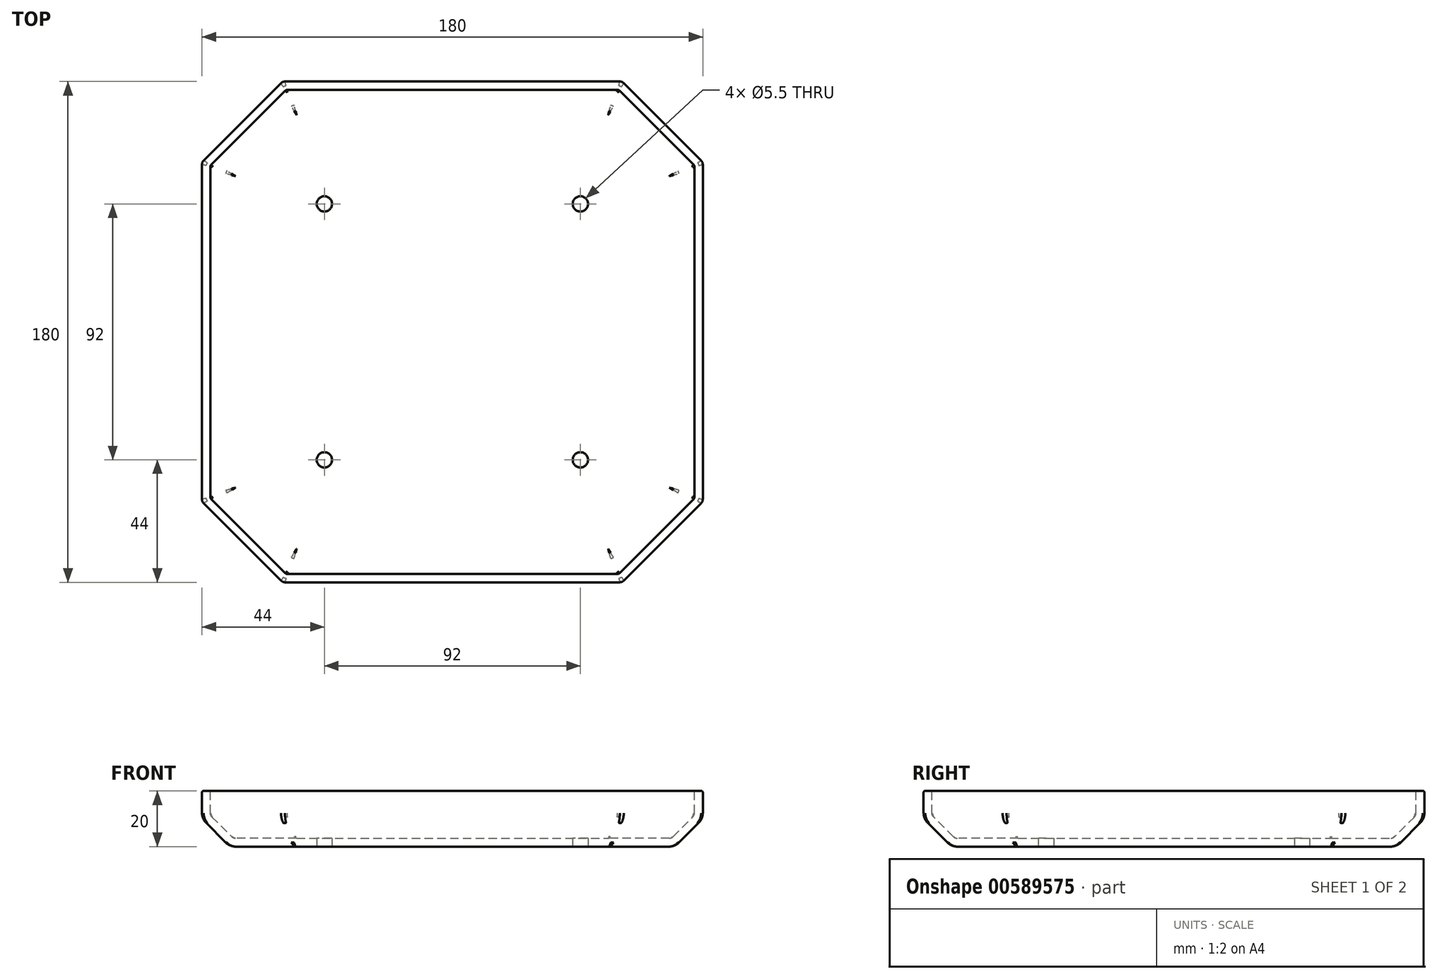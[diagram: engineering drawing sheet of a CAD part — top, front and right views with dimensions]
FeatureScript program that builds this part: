
annotation { "Feature Type Name" : "Feature", "Feature Type Description" : "" }
export const myFeature = defineFeature(function(context is Context, id is Id, definition is map)
    precondition{}
    {
        {
            var Q0;
            Q0=qCreatedBy(makeId("Top.planeOp"),FACE);
            var sketch = newSketch(context, id + "F0", { "sketchPlane" : qUnion([Q0])});
            skLineSegment(sketch, "E0.bottom", {"start": v(-61, 90) * mm, "end": v(61, 90) * mm});
            skLineSegment(sketch, "E0.top", {"start": v(-61, -90) * mm, "end": v(61, -90) * mm});
            skLineSegment(sketch, "E0.left", {"start": v(-90, 61) * mm, "end": v(-90, -61) * mm});
            skLineSegment(sketch, "E0.right", {"start": v(90, 61) * mm, "end": v(90, -61) * mm});
            skLineSegment(sketch, "E1", {"start": v(0, 156.9) * mm, "end": v(0, -146.72) * mm, "construction": true});
            skLineSegment(sketch, "E2", {"start": v(-149.43, 0) * mm, "end": v(169.81, 0) * mm, "construction": true});
            skLineSegment(sketch, "E3", {"start": v(-90, 61) * mm, "end": v(-61, 90) * mm});
            skLineSegment(sketch, "E4", {"start": v(-90, -61) * mm, "end": v(-61, -90) * mm});
            skLineSegment(sketch, "E5", {"start": v(61, -90) * mm, "end": v(90, -61) * mm});
            skLineSegment(sketch, "E6", {"start": v(61, 90) * mm, "end": v(90, 61) * mm});
            skPoint(sketch, "E7.orphan", {"position": v(-90, 90) * mm});
            skPoint(sketch, "E8.orphan", {"position": v(90, 90) * mm});
            skPoint(sketch, "E9.orphan", {"position": v(90, -90) * mm});
            skPoint(sketch, "E10.orphan", {"position": v(-90, -90) * mm});
            skSolve(sketch);
        }
        {
            var Q0;
            Q0=qSketchRegion(id+"F0",true);
            extrude(context, id + "F1", {"entities" : qUnion([Q0]), "depth" : 20 * mm, "offsetDistance" : 25 * mm});
        }
        {
            var Q0;
            Q0=makeQuery(id+"F1.opExtrude","CAP_EDGE",EDGE,{"disambiguationData":[OSD([sQuery(id+"F0.wireOp",EDGE,"E0.top")])],"isStart":true});
            var Q1;
            Q1=makeQuery(id+"F1.opExtrude","CAP_EDGE",EDGE,{"disambiguationData":[OSD([sQuery(id+"F0.wireOp",EDGE,"E4")])],"isStart":true});
            var Q2;
            Q2=makeQuery(id+"F1.opExtrude","CAP_EDGE",EDGE,{"disambiguationData":[OSD([sQuery(id+"F0.wireOp",EDGE,"E0.left")])],"isStart":true});
            var Q3;
            Q3=makeQuery(id+"F1.opExtrude","CAP_EDGE",EDGE,{"disambiguationData":[OSD([sQuery(id+"F0.wireOp",EDGE,"E3")])],"isStart":true});
            var Q4;
            Q4=makeQuery(id+"F1.opExtrude","CAP_EDGE",EDGE,{"disambiguationData":[OSD([sQuery(id+"F0.wireOp",EDGE,"E0.bottom")])],"isStart":true});
            var Q5;
            Q5=makeQuery(id+"F1.opExtrude","CAP_EDGE",EDGE,{"disambiguationData":[OSD([sQuery(id+"F0.wireOp",EDGE,"E6")])],"isStart":true});
            var Q6;
            Q6=makeQuery(id+"F1.opExtrude","CAP_EDGE",EDGE,{"disambiguationData":[OSD([sQuery(id+"F0.wireOp",EDGE,"E0.right")])],"isStart":true});
            var Q7;
            Q7=makeQuery(id+"F1.opExtrude","CAP_EDGE",EDGE,{"disambiguationData":[OSD([sQuery(id+"F0.wireOp",EDGE,"E5")])],"isStart":true});
            chamfer(context, id + "F2", {"entities" : qUnion([Q0, Q1, Q2, Q3, Q4, Q5, Q6, Q7]), "chamferType" : ChamferType.TWO_OFFSETS, "width1" : 10 * mm, "oppositeDirection" : true, "width2" : 10 * mm, "tangentPropagation" : true});
        }
        {
            var Q0;
            {var subQ0=sQuery(id+"F0.wireOp",EDGE,"E6");Q0=makeQuery(id+"F2.opChamfer","BLEND_EDGE",EDGE,{"blendedFrom":[makeQuery(id+"F1.opExtrude","CAP_EDGE",EDGE,{"disambiguationData":[OSD([subQ0])],"isStart":true}),makeQuery(id+"F1.opExtrude","SWEPT_FACE",FACE,{"disambiguationData":[OSD([subQ0])]})],"blendedInto":[makeQuery(id+"F1.opExtrude","SWEPT_FACE",FACE,{"disambiguationData":[OSD([subQ0])]})]});}
            var Q1;
            {var subQ0=sQuery(id+"F0.wireOp",EDGE,"E0.right");Q1=makeQuery(id+"F2.opChamfer","BLEND_EDGE",EDGE,{"blendedFrom":[makeQuery(id+"F1.opExtrude","CAP_EDGE",EDGE,{"disambiguationData":[OSD([subQ0])],"isStart":true}),makeQuery(id+"F1.opExtrude","SWEPT_FACE",FACE,{"disambiguationData":[OSD([subQ0])]})],"blendedInto":[makeQuery(id+"F1.opExtrude","SWEPT_FACE",FACE,{"disambiguationData":[OSD([subQ0])]})]});}
            var Q2;
            {var subQ0=sQuery(id+"F0.wireOp",EDGE,"E5");Q2=makeQuery(id+"F2.opChamfer","BLEND_EDGE",EDGE,{"blendedFrom":[makeQuery(id+"F1.opExtrude","CAP_EDGE",EDGE,{"disambiguationData":[OSD([subQ0])],"isStart":true}),makeQuery(id+"F1.opExtrude","SWEPT_FACE",FACE,{"disambiguationData":[OSD([subQ0])]})],"blendedInto":[makeQuery(id+"F1.opExtrude","SWEPT_FACE",FACE,{"disambiguationData":[OSD([subQ0])]})]});}
            var Q3;
            {var subQ0=sQuery(id+"F0.wireOp",EDGE,"E0.top");Q3=makeQuery(id+"F2.opChamfer","BLEND_EDGE",EDGE,{"blendedFrom":[makeQuery(id+"F1.opExtrude","CAP_EDGE",EDGE,{"disambiguationData":[OSD([subQ0])],"isStart":true}),makeQuery(id+"F1.opExtrude","SWEPT_FACE",FACE,{"disambiguationData":[OSD([subQ0])]})],"blendedInto":[makeQuery(id+"F1.opExtrude","SWEPT_FACE",FACE,{"disambiguationData":[OSD([subQ0])]})]});}
            var Q4;
            {var subQ0=sQuery(id+"F0.wireOp",EDGE,"E4");Q4=makeQuery(id+"F2.opChamfer","BLEND_EDGE",EDGE,{"blendedFrom":[makeQuery(id+"F1.opExtrude","CAP_EDGE",EDGE,{"disambiguationData":[OSD([subQ0])],"isStart":true}),makeQuery(id+"F1.opExtrude","SWEPT_FACE",FACE,{"disambiguationData":[OSD([subQ0])]})],"blendedInto":[makeQuery(id+"F1.opExtrude","SWEPT_FACE",FACE,{"disambiguationData":[OSD([subQ0])]})]});}
            var Q5;
            {var subQ0=sQuery(id+"F0.wireOp",EDGE,"E0.left");Q5=makeQuery(id+"F2.opChamfer","BLEND_EDGE",EDGE,{"blendedFrom":[makeQuery(id+"F1.opExtrude","CAP_EDGE",EDGE,{"disambiguationData":[OSD([subQ0])],"isStart":true}),makeQuery(id+"F1.opExtrude","SWEPT_FACE",FACE,{"disambiguationData":[OSD([subQ0])]})],"blendedInto":[makeQuery(id+"F1.opExtrude","SWEPT_FACE",FACE,{"disambiguationData":[OSD([subQ0])]})]});}
            var Q6;
            {var subQ0=sQuery(id+"F0.wireOp",EDGE,"E3");Q6=makeQuery(id+"F2.opChamfer","BLEND_EDGE",EDGE,{"blendedFrom":[makeQuery(id+"F1.opExtrude","CAP_EDGE",EDGE,{"disambiguationData":[OSD([subQ0])],"isStart":true}),makeQuery(id+"F1.opExtrude","SWEPT_FACE",FACE,{"disambiguationData":[OSD([subQ0])]})],"blendedInto":[makeQuery(id+"F1.opExtrude","SWEPT_FACE",FACE,{"disambiguationData":[OSD([subQ0])]})]});}
            var Q7;
            {var subQ0=sQuery(id+"F0.wireOp",EDGE,"E0.bottom");Q7=makeQuery(id+"F2.opChamfer","BLEND_EDGE",EDGE,{"blendedFrom":[makeQuery(id+"F1.opExtrude","CAP_EDGE",EDGE,{"disambiguationData":[OSD([subQ0])],"isStart":true}),makeQuery(id+"F1.opExtrude","SWEPT_FACE",FACE,{"disambiguationData":[OSD([subQ0])]})],"blendedInto":[makeQuery(id+"F1.opExtrude","SWEPT_FACE",FACE,{"disambiguationData":[OSD([subQ0])]})]});}
            fillet(context, id + "F3", {"entities" : qUnion([Q0, Q1, Q2, Q3, Q4, Q5, Q6, Q7]), "radius" : 5 * mm, "tangentPropagation" : true, "allowEdgeOverflow" : false});
        }
        {
            var Q0;
            Q0=makeQuery(id+"FPPhOqti1fwxr9W_1.boolean.opBoolean","MERGE",EDGE,{"derivedFrom":[makeQuery(id+"F1.opExtrude","SWEPT_EDGE",EDGE,{"disambiguationData":[OSD([sQuery(id+"F0.wireOp",EDGE,"E0.bottom"),sQuery(id+"F0.wireOp",EDGE,"E6")])]}),makeQuery(id+"FPPhOqti1fwxr9W_1.opExtrude","SWEPT_EDGE",EDGE,{"disambiguationData":[OSD([sQuery(id+"Fz5JRvEoveer3CH_1.wireOp",EDGE,"2a3d6910-861b-4cd5-9b03-4775f4baa4122.MirrorCS"),sQuery(id+"Fz5JRvEoveer3CH_1.wireOp",EDGE,"2a3d6910-861b-4cd5-9b03-4775f4baa4128.MirrorCS")])]})]});
            var Q1;
            Q1=makeQuery(id+"FPPhOqti1fwxr9W_1.boolean.opBoolean","MERGE",EDGE,{"derivedFrom":[makeQuery(id+"F1.opExtrude","SWEPT_EDGE",EDGE,{"disambiguationData":[OSD([sQuery(id+"F0.wireOp",EDGE,"E0.right"),sQuery(id+"F0.wireOp",EDGE,"E6")])]}),makeQuery(id+"FPPhOqti1fwxr9W_1.opExtrude","SWEPT_EDGE",EDGE,{"disambiguationData":[OSD([sQuery(id+"Fz5JRvEoveer3CH_1.wireOp",EDGE,"2a3d6910-861b-4cd5-9b03-4775f4baa4123.MirrorCS"),sQuery(id+"Fz5JRvEoveer3CH_1.wireOp",EDGE,"2a3d6910-861b-4cd5-9b03-4775f4baa4128.MirrorCS")])]})]});
            var Q2;
            Q2=makeQuery(id+"FPPhOqti1fwxr9W_1.boolean.opBoolean","MERGE",EDGE,{"derivedFrom":[makeQuery(id+"F1.opExtrude","SWEPT_EDGE",EDGE,{"disambiguationData":[OSD([sQuery(id+"F0.wireOp",EDGE,"E0.bottom"),sQuery(id+"F0.wireOp",EDGE,"E3")])]}),makeQuery(id+"FPPhOqti1fwxr9W_1.opExtrude","SWEPT_EDGE",EDGE,{"disambiguationData":[OSD([sQuery(id+"Fz5JRvEoveer3CH_1.wireOp",EDGE,"ed581da2-8291-48fe-b3ed-69cef9aa138a21.MirrorCS"),sQuery(id+"Fz5JRvEoveer3CH_1.wireOp",EDGE,"ed581da2-8291-48fe-b3ed-69cef9aa138a29.MirrorCS")])]})]});
            var Q3;
            Q3=makeQuery(id+"FPPhOqti1fwxr9W_1.boolean.opBoolean","MERGE",EDGE,{"derivedFrom":[makeQuery(id+"F1.opExtrude","SWEPT_EDGE",EDGE,{"disambiguationData":[OSD([sQuery(id+"F0.wireOp",EDGE,"E0.right"),sQuery(id+"F0.wireOp",EDGE,"E5")])]}),makeQuery(id+"FPPhOqti1fwxr9W_1.opExtrude","SWEPT_EDGE",EDGE,{"disambiguationData":[OSD([sQuery(id+"Fz5JRvEoveer3CH_1.wireOp",EDGE,"ipMyZAYz-hxr7-lcg5-t2S8-iXpkemTBpe0R"),sQuery(id+"Fz5JRvEoveer3CH_1.wireOp",EDGE,"9DZyxgSF-dPzx-yPfH-Wviq-A2BslGx0M5Kc")])]})]});
            var Q4;
            Q4=makeQuery(id+"F2.opChamfer","BLEND_EDGE",EDGE,{"blendedFrom":[makeQuery(id+"F1.opExtrude","CAP_EDGE",EDGE,{"disambiguationData":[OSD([sQuery(id+"F0.wireOp",EDGE,"E0.top")])],"isStart":true}),makeQuery(id+"F1.opExtrude","CAP_EDGE",EDGE,{"disambiguationData":[OSD([sQuery(id+"F0.wireOp",EDGE,"E5")])],"isStart":true})],"blendedInto":[]});
            var Q5;
            Q5=makeQuery(id+"F2.opChamfer","BLEND_EDGE",EDGE,{"blendedFrom":[makeQuery(id+"F1.opExtrude","CAP_EDGE",EDGE,{"disambiguationData":[OSD([sQuery(id+"F0.wireOp",EDGE,"E0.top")])],"isStart":true}),makeQuery(id+"F1.opExtrude","CAP_EDGE",EDGE,{"disambiguationData":[OSD([sQuery(id+"F0.wireOp",EDGE,"E4")])],"isStart":true})],"blendedInto":[]});
            var Q6;
            Q6=makeQuery(id+"F2.opChamfer","BLEND_EDGE",EDGE,{"blendedFrom":[makeQuery(id+"F1.opExtrude","CAP_EDGE",EDGE,{"disambiguationData":[OSD([sQuery(id+"F0.wireOp",EDGE,"E0.left")])],"isStart":true}),makeQuery(id+"F1.opExtrude","CAP_EDGE",EDGE,{"disambiguationData":[OSD([sQuery(id+"F0.wireOp",EDGE,"E4")])],"isStart":true})],"blendedInto":[]});
            var Q7;
            Q7=makeQuery(id+"F2.opChamfer","BLEND_EDGE",EDGE,{"blendedFrom":[makeQuery(id+"F1.opExtrude","CAP_EDGE",EDGE,{"disambiguationData":[OSD([sQuery(id+"F0.wireOp",EDGE,"E0.left")])],"isStart":true}),makeQuery(id+"F1.opExtrude","CAP_EDGE",EDGE,{"disambiguationData":[OSD([sQuery(id+"F0.wireOp",EDGE,"E3")])],"isStart":true})],"blendedInto":[]});
            fillet(context, id + "F4", {"entities" : qUnion([Q0, Q1, Q2, Q3, Q4, Q5, Q6, Q7]), "radius" : 2 * mm, "tangentPropagation" : true, "allowEdgeOverflow" : false});
        }
        {
            var Q0;
            {var subQ0=sQuery(id+"F0.wireOp",EDGE,"E0.left");Q0=makeQuery(id+"F2.opChamfer","BLEND_EDGE",EDGE,{"blendedFrom":[makeQuery(id+"F1.opExtrude","CAP_EDGE",EDGE,{"disambiguationData":[OSD([subQ0])],"isStart":true}),makeQuery(id+"F1.opExtrude","CAP_FACE",FACE,{"disambiguationData":[OSD([sQuery(id+"F0.wireOp",EDGE,"E0.bottom"),sQuery(id+"F0.wireOp",EDGE,"E0.top"),subQ0,sQuery(id+"F0.wireOp",EDGE,"E0.right"),sQuery(id+"F0.wireOp",EDGE,"E3"),sQuery(id+"F0.wireOp",EDGE,"E4"),sQuery(id+"F0.wireOp",EDGE,"E5"),sQuery(id+"F0.wireOp",EDGE,"E6")])],"isStart":true})],"blendedInto":[makeQuery(id+"F1.opExtrude","CAP_FACE",FACE,{"disambiguationData":[OSD([sQuery(id+"F0.wireOp",EDGE,"E0.bottom"),sQuery(id+"F0.wireOp",EDGE,"E0.top"),subQ0,sQuery(id+"F0.wireOp",EDGE,"E0.right"),sQuery(id+"F0.wireOp",EDGE,"E3"),sQuery(id+"F0.wireOp",EDGE,"E4"),sQuery(id+"F0.wireOp",EDGE,"E5"),sQuery(id+"F0.wireOp",EDGE,"E6")])],"isStart":true})]});}
            fillet(context, id + "F5", {"entities" : qUnion([Q0]), "radius" : 5 * mm, "tangentPropagation" : true, "allowEdgeOverflow" : false});
        }
        {
            var Q0;
            Q0=makeQuery(id+"F1.opExtrude","CAP_FACE",FACE,{"disambiguationData":[OSD([sQuery(id+"F0.wireOp",EDGE,"E0.bottom"),sQuery(id+"F0.wireOp",EDGE,"E0.top"),sQuery(id+"F0.wireOp",EDGE,"E0.left"),sQuery(id+"F0.wireOp",EDGE,"E0.right"),sQuery(id+"F0.wireOp",EDGE,"E3"),sQuery(id+"F0.wireOp",EDGE,"E4"),sQuery(id+"F0.wireOp",EDGE,"E5"),sQuery(id+"F0.wireOp",EDGE,"E6")])],"isStart":false});
            shell(context, id + "F6", {"entities" : qUnion([Q0]), "thickness" : 3 * mm});
        }
        {
            var Q0;
            Q0=makeQuery(id+"F1.opExtrude","CAP_FACE",FACE,{"disambiguationData":[OSD([sQuery(id+"F0.wireOp",EDGE,"E0.bottom"),sQuery(id+"F0.wireOp",EDGE,"E0.top"),sQuery(id+"F0.wireOp",EDGE,"E0.left"),sQuery(id+"F0.wireOp",EDGE,"E0.right"),sQuery(id+"F0.wireOp",EDGE,"E3"),sQuery(id+"F0.wireOp",EDGE,"E4"),sQuery(id+"F0.wireOp",EDGE,"E5"),sQuery(id+"F0.wireOp",EDGE,"E6")])],"isStart":true});
            var sketch = newSketch(context, id + "F7", { "sketchPlane" : qUnion([Q0])});
            skLineSegment(sketch, "E11", {"start": v(0, 77.93) * mm, "end": v(0, -77.93) * mm, "construction": true});
            skLineSegment(sketch, "E12", {"start": v(-77.93, 0) * mm, "end": v(77.93, 0) * mm, "construction": true});
            skLineSegment(sketch, "E13", {"start": v(-66.96, -66.96) * mm, "end": v(66.96, 66.96) * mm, "construction": true});
            skLineSegment(sketch, "E14", {"start": v(-66.96, 66.96) * mm, "end": v(66.96, -66.96) * mm, "construction": true});
            skCircle(sketch, "E15", {"center": v(-46, -46) * mm, "radius": 2.75 * mm});
            skCircle(sketch, "E16", {"center": v(-46, 46) * mm, "radius": 2.75 * mm});
            skCircle(sketch, "E17", {"center": v(46, 46) * mm, "radius": 2.75 * mm});
            skCircle(sketch, "E18", {"center": v(46, -46) * mm, "radius": 2.75 * mm});
            skSolve(sketch);
        }
        {
            var Q0;
            Q0=qSketchRegion(id+"F7",true);
            extrude(context, id + "F8", {"entities" : qUnion([Q0]), "operationType" : NewBodyOperationType.REMOVE, "oppositeDirection" : true, "depth" : 25 * mm});
        }
        {
            var Q0;
            Q0=makeQuery(id+"F1.opExtrude","CAP_EDGE",EDGE,{"disambiguationData":[OSD([sQuery(id+"F0.wireOp",EDGE,"E0.bottom")])],"isStart":false});
            fillet(context, id + "F9", {"entities" : qUnion([Q0]), "radius" : 0.5 * mm, "tangentPropagation" : true, "allowEdgeOverflow" : false});
        }
        {
            var Q0;
            {var subQ0=sQuery(id+"Fz5JRvEoveer3CH_1.wireOp",EDGE,"2a3d6910-861b-4cd5-9b03-4775f4baa4123.MirrorCS");var subQ1=sQuery(id+"Fz5JRvEoveer3CH_1.wireOp",EDGE,"9DZyxgSF-dPzx-yPfH-Wviq-A2BslGx0M5Kc");var subQ2=sQuery(id+"F0.wireOp",EDGE,"E0.right");var subQ4=sQuery(id+"Fz5JRvEoveer3CH_1.wireOp",EDGE,"2a3d6910-861b-4cd5-9b03-4775f4baa4128.MirrorCS");var subQ5=sQuery(id+"F0.wireOp",EDGE,"E6");var subQ7=makeQuery(id+"F6.opShell","OFFSET_EDGE",EDGE,{"disambiguationData":[OSD([subQ2,subQ5,subQ1,subQ0,subQ4])]});Q0=makeQuery(id+"FdvM71XXdWx955j_1.boolean.opBoolean","MERGE",EDGE,{"derivedFrom":[makeQuery(id+"Fx6GF23n7295V4c_1.boolean.opBoolean","SPLIT",EDGE,{"disambiguationData":[TD([makeQuery(id+"Fx6GF23n7295V4c_1.opExtrude","SWEPT_FACE",FACE,{"disambiguationData":[OSD([sQuery(id+"F88hl3kOj6oPiEs_1.wireOp",EDGE,"Me13D1SK-nVIm-EUZ4-u9ei-o20qw3bNrjn4.top")])]})])],"derivedFrom":subQ7}),makeQuery(id+"Fx6GF23n7295V4c_1.boolean.opBoolean","SPLIT",EDGE,{"disambiguationData":[TD([makeQuery(id+"Fx6GF23n7295V4c_1.opExtrude","SWEPT_FACE",FACE,{"disambiguationData":[OSD([sQuery(id+"F88hl3kOj6oPiEs_1.wireOp",EDGE,"SEwAjyqW-bpiv-PUip-ikyk-NmgX0KRneyY1.bottom")])]})])],"derivedFrom":subQ7}),makeQuery(id+"Fx6GF23n7295V4c_1.boolean.opBoolean","SPLIT",EDGE,{"disambiguationData":[TD([makeQuery(id+"Fx6GF23n7295V4c_1.opExtrude","SWEPT_FACE",FACE,{"disambiguationData":[OSD([sQuery(id+"F88hl3kOj6oPiEs_1.wireOp",EDGE,"Me13D1SK-nVIm-EUZ4-u9ei-o20qw3bNrjn4.bottom")])]})])],"derivedFrom":subQ7}),makeQuery(id+"FdvM71XXdWx955j_1.opExtrude","SWEPT_EDGE",EDGE,{"disambiguationData":[OSD([sQuery(id+"FbjQCpLspRogReH_1.wireOp",EDGE,"f59d4a9d-c009-47c2-b376-d2920ef91a05.8"),sQuery(id+"FbjQCpLspRogReH_1.wireOp",EDGE,"bRIcUt5c-2wkI-2ICm-p1hK-NbXWkc9YcS5q")])]})]});}
            var Q1;
            {var subQ0=sQuery(id+"Fz5JRvEoveer3CH_1.wireOp",EDGE,"ed581da2-8291-48fe-b3ed-69cef9aa138a21.MirrorCS");var subQ1=sQuery(id+"Fz5JRvEoveer3CH_1.wireOp",EDGE,"2a3d6910-861b-4cd5-9b03-4775f4baa4122.MirrorCS");var subQ2=sQuery(id+"F0.wireOp",EDGE,"E0.bottom");var subQ4=sQuery(id+"Fz5JRvEoveer3CH_1.wireOp",EDGE,"2a3d6910-861b-4cd5-9b03-4775f4baa4128.MirrorCS");var subQ5=sQuery(id+"F0.wireOp",EDGE,"E6");var subQ7=makeQuery(id+"F6.opShell","OFFSET_EDGE",EDGE,{"disambiguationData":[OSD([subQ2,subQ5,subQ1,subQ4,subQ0])]});Q1=makeQuery(id+"FdvM71XXdWx955j_1.boolean.opBoolean","MERGE",EDGE,{"derivedFrom":[makeQuery(id+"Fx6GF23n7295V4c_1.boolean.opBoolean","SPLIT",EDGE,{"disambiguationData":[TD([makeQuery(id+"Fx6GF23n7295V4c_1.opExtrude","SWEPT_FACE",FACE,{"disambiguationData":[OSD([sQuery(id+"F88hl3kOj6oPiEs_1.wireOp",EDGE,"Me13D1SK-nVIm-EUZ4-u9ei-o20qw3bNrjn4.top")])]})])],"derivedFrom":subQ7}),makeQuery(id+"Fx6GF23n7295V4c_1.boolean.opBoolean","SPLIT",EDGE,{"disambiguationData":[TD([makeQuery(id+"Fx6GF23n7295V4c_1.opExtrude","SWEPT_FACE",FACE,{"disambiguationData":[OSD([sQuery(id+"F88hl3kOj6oPiEs_1.wireOp",EDGE,"SEwAjyqW-bpiv-PUip-ikyk-NmgX0KRneyY1.bottom")])]})])],"derivedFrom":subQ7}),makeQuery(id+"Fx6GF23n7295V4c_1.boolean.opBoolean","SPLIT",EDGE,{"disambiguationData":[TD([makeQuery(id+"Fx6GF23n7295V4c_1.opExtrude","SWEPT_FACE",FACE,{"disambiguationData":[OSD([sQuery(id+"F88hl3kOj6oPiEs_1.wireOp",EDGE,"Me13D1SK-nVIm-EUZ4-u9ei-o20qw3bNrjn4.bottom")])]})])],"derivedFrom":subQ7}),makeQuery(id+"FdvM71XXdWx955j_1.opExtrude","SWEPT_EDGE",EDGE,{"disambiguationData":[OSD([sQuery(id+"FbjQCpLspRogReH_1.wireOp",EDGE,"f59d4a9d-c009-47c2-b376-d2920ef91a05.4"),sQuery(id+"FbjQCpLspRogReH_1.wireOp",EDGE,"bRIcUt5c-2wkI-2ICm-p1hK-NbXWkc9YcS5q")])]})]});}
            var Q2;
            {var subQ0=sQuery(id+"Fz5JRvEoveer3CH_1.wireOp",EDGE,"2a3d6910-861b-4cd5-9b03-4775f4baa4123.MirrorCS");var subQ1=sQuery(id+"Fz5JRvEoveer3CH_1.wireOp",EDGE,"9DZyxgSF-dPzx-yPfH-Wviq-A2BslGx0M5Kc");var subQ2=sQuery(id+"F0.wireOp",EDGE,"E0.right");var subQ4=sQuery(id+"Fz5JRvEoveer3CH_1.wireOp",EDGE,"ipMyZAYz-hxr7-lcg5-t2S8-iXpkemTBpe0R");var subQ5=sQuery(id+"F0.wireOp",EDGE,"E5");var subQ7=makeQuery(id+"F6.opShell","OFFSET_EDGE",EDGE,{"disambiguationData":[OSD([subQ2,subQ5,subQ4,subQ1,subQ0])]});Q2=makeQuery(id+"FdvM71XXdWx955j_1.boolean.opBoolean","MERGE",EDGE,{"derivedFrom":[makeQuery(id+"Fx6GF23n7295V4c_1.boolean.opBoolean","SPLIT",EDGE,{"disambiguationData":[TD([makeQuery(id+"Fx6GF23n7295V4c_1.opExtrude","SWEPT_FACE",FACE,{"disambiguationData":[OSD([sQuery(id+"F88hl3kOj6oPiEs_1.wireOp",EDGE,"Me13D1SK-nVIm-EUZ4-u9ei-o20qw3bNrjn4.top")])]})])],"derivedFrom":subQ7}),makeQuery(id+"Fx6GF23n7295V4c_1.boolean.opBoolean","SPLIT",EDGE,{"disambiguationData":[TD([makeQuery(id+"Fx6GF23n7295V4c_1.opExtrude","SWEPT_FACE",FACE,{"disambiguationData":[OSD([sQuery(id+"F88hl3kOj6oPiEs_1.wireOp",EDGE,"SEwAjyqW-bpiv-PUip-ikyk-NmgX0KRneyY1.bottom")])]})])],"derivedFrom":subQ7}),makeQuery(id+"Fx6GF23n7295V4c_1.boolean.opBoolean","SPLIT",EDGE,{"disambiguationData":[TD([makeQuery(id+"Fx6GF23n7295V4c_1.opExtrude","SWEPT_FACE",FACE,{"disambiguationData":[OSD([sQuery(id+"F88hl3kOj6oPiEs_1.wireOp",EDGE,"Me13D1SK-nVIm-EUZ4-u9ei-o20qw3bNrjn4.bottom")])]})])],"derivedFrom":subQ7}),makeQuery(id+"FdvM71XXdWx955j_1.opExtrude","SWEPT_EDGE",EDGE,{"disambiguationData":[OSD([sQuery(id+"FbjQCpLspRogReH_1.wireOp",EDGE,"f59d4a9d-c009-47c2-b376-d2920ef91a05.8"),sQuery(id+"FbjQCpLspRogReH_1.wireOp",EDGE,"k8ZdSqg6-Hz3y-xcz6-AWJW-23JSN5h7mf7L")])]})]});}
            var Q3;
            {var subQ0=sQuery(id+"Fz5JRvEoveer3CH_1.wireOp",EDGE,"ed581da2-8291-48fe-b3ed-69cef9aa138a6.MirrorCS");var subQ1=sQuery(id+"Fz5JRvEoveer3CH_1.wireOp",EDGE,"H1DbfBLt-s3tm-ktFB-kuIm-WvYZTs067Ftm");var subQ2=sQuery(id+"F0.wireOp",EDGE,"E0.top");var subQ4=sQuery(id+"Fz5JRvEoveer3CH_1.wireOp",EDGE,"ipMyZAYz-hxr7-lcg5-t2S8-iXpkemTBpe0R");var subQ5=sQuery(id+"F0.wireOp",EDGE,"E5");var subQ7=makeQuery(id+"F6.opShell","OFFSET_EDGE",EDGE,{"disambiguationData":[OSD([subQ2,subQ5,subQ4,subQ1,subQ0])]});Q3=makeQuery(id+"FdvM71XXdWx955j_1.boolean.opBoolean","MERGE",EDGE,{"derivedFrom":[makeQuery(id+"Fx6GF23n7295V4c_1.boolean.opBoolean","SPLIT",EDGE,{"disambiguationData":[TD([makeQuery(id+"Fx6GF23n7295V4c_1.opExtrude","SWEPT_FACE",FACE,{"disambiguationData":[OSD([sQuery(id+"F88hl3kOj6oPiEs_1.wireOp",EDGE,"Me13D1SK-nVIm-EUZ4-u9ei-o20qw3bNrjn4.top")])]})])],"derivedFrom":subQ7}),makeQuery(id+"Fx6GF23n7295V4c_1.boolean.opBoolean","SPLIT",EDGE,{"disambiguationData":[TD([makeQuery(id+"Fx6GF23n7295V4c_1.opExtrude","SWEPT_FACE",FACE,{"disambiguationData":[OSD([sQuery(id+"F88hl3kOj6oPiEs_1.wireOp",EDGE,"SEwAjyqW-bpiv-PUip-ikyk-NmgX0KRneyY1.bottom")])]})])],"derivedFrom":subQ7}),makeQuery(id+"Fx6GF23n7295V4c_1.boolean.opBoolean","SPLIT",EDGE,{"disambiguationData":[TD([makeQuery(id+"Fx6GF23n7295V4c_1.opExtrude","SWEPT_FACE",FACE,{"disambiguationData":[OSD([sQuery(id+"F88hl3kOj6oPiEs_1.wireOp",EDGE,"Me13D1SK-nVIm-EUZ4-u9ei-o20qw3bNrjn4.bottom")])]})])],"derivedFrom":subQ7}),makeQuery(id+"FdvM71XXdWx955j_1.opExtrude","SWEPT_EDGE",EDGE,{"disambiguationData":[OSD([sQuery(id+"FbjQCpLspRogReH_1.wireOp",EDGE,"f59d4a9d-c009-47c2-b376-d2920ef91a05.12"),sQuery(id+"FbjQCpLspRogReH_1.wireOp",EDGE,"k8ZdSqg6-Hz3y-xcz6-AWJW-23JSN5h7mf7L")])]})]});}
            var Q4;
            {var subQ0=sQuery(id+"Fz5JRvEoveer3CH_1.wireOp",EDGE,"ed581da2-8291-48fe-b3ed-69cef9aa138a6.MirrorCS");var subQ1=sQuery(id+"Fz5JRvEoveer3CH_1.wireOp",EDGE,"H1DbfBLt-s3tm-ktFB-kuIm-WvYZTs067Ftm");var subQ2=sQuery(id+"F0.wireOp",EDGE,"E0.top");var subQ4=sQuery(id+"Fz5JRvEoveer3CH_1.wireOp",EDGE,"ed581da2-8291-48fe-b3ed-69cef9aa138a20.MirrorCS");var subQ5=sQuery(id+"F0.wireOp",EDGE,"E4");var subQ7=makeQuery(id+"F6.opShell","OFFSET_EDGE",EDGE,{"disambiguationData":[OSD([subQ2,subQ5,subQ1,subQ0,subQ4])]});Q4=makeQuery(id+"FdvM71XXdWx955j_1.boolean.opBoolean","MERGE",EDGE,{"derivedFrom":[makeQuery(id+"Fx6GF23n7295V4c_1.boolean.opBoolean","SPLIT",EDGE,{"disambiguationData":[TD([makeQuery(id+"Fx6GF23n7295V4c_1.opExtrude","SWEPT_FACE",FACE,{"disambiguationData":[OSD([sQuery(id+"F88hl3kOj6oPiEs_1.wireOp",EDGE,"Me13D1SK-nVIm-EUZ4-u9ei-o20qw3bNrjn4.top")])]})])],"derivedFrom":subQ7}),makeQuery(id+"Fx6GF23n7295V4c_1.boolean.opBoolean","SPLIT",EDGE,{"disambiguationData":[TD([makeQuery(id+"Fx6GF23n7295V4c_1.opExtrude","SWEPT_FACE",FACE,{"disambiguationData":[OSD([sQuery(id+"F88hl3kOj6oPiEs_1.wireOp",EDGE,"SEwAjyqW-bpiv-PUip-ikyk-NmgX0KRneyY1.bottom")])]})])],"derivedFrom":subQ7}),makeQuery(id+"Fx6GF23n7295V4c_1.boolean.opBoolean","SPLIT",EDGE,{"disambiguationData":[TD([makeQuery(id+"Fx6GF23n7295V4c_1.opExtrude","SWEPT_FACE",FACE,{"disambiguationData":[OSD([sQuery(id+"F88hl3kOj6oPiEs_1.wireOp",EDGE,"Me13D1SK-nVIm-EUZ4-u9ei-o20qw3bNrjn4.bottom")])]})])],"derivedFrom":subQ7}),makeQuery(id+"FdvM71XXdWx955j_1.opExtrude","SWEPT_EDGE",EDGE,{"disambiguationData":[OSD([sQuery(id+"FbjQCpLspRogReH_1.wireOp",EDGE,"f59d4a9d-c009-47c2-b376-d2920ef91a05.12"),sQuery(id+"FbjQCpLspRogReH_1.wireOp",EDGE,"yJWQzcis-0yOI-6z6T-26nz-SCj8SExaznUa")])]})]});}
            var Q5;
            {var subQ0=sQuery(id+"Fz5JRvEoveer3CH_1.wireOp",EDGE,"ed581da2-8291-48fe-b3ed-69cef9aa138a18.MirrorCS");var subQ1=sQuery(id+"Fz5JRvEoveer3CH_1.wireOp",EDGE,"ed581da2-8291-48fe-b3ed-69cef9aa138a14.MirrorCS");var subQ2=sQuery(id+"F0.wireOp",EDGE,"E0.left");var subQ4=sQuery(id+"Fz5JRvEoveer3CH_1.wireOp",EDGE,"ed581da2-8291-48fe-b3ed-69cef9aa138a20.MirrorCS");var subQ5=sQuery(id+"F0.wireOp",EDGE,"E4");var subQ7=makeQuery(id+"F6.opShell","OFFSET_EDGE",EDGE,{"disambiguationData":[OSD([subQ2,subQ5,subQ1,subQ0,subQ4])]});Q5=makeQuery(id+"FdvM71XXdWx955j_1.boolean.opBoolean","MERGE",EDGE,{"derivedFrom":[makeQuery(id+"Fx6GF23n7295V4c_1.boolean.opBoolean","SPLIT",EDGE,{"disambiguationData":[TD([makeQuery(id+"Fx6GF23n7295V4c_1.opExtrude","SWEPT_FACE",FACE,{"disambiguationData":[OSD([sQuery(id+"F88hl3kOj6oPiEs_1.wireOp",EDGE,"Me13D1SK-nVIm-EUZ4-u9ei-o20qw3bNrjn4.top")])]})])],"derivedFrom":subQ7}),makeQuery(id+"Fx6GF23n7295V4c_1.boolean.opBoolean","SPLIT",EDGE,{"disambiguationData":[TD([makeQuery(id+"Fx6GF23n7295V4c_1.opExtrude","SWEPT_FACE",FACE,{"disambiguationData":[OSD([sQuery(id+"F88hl3kOj6oPiEs_1.wireOp",EDGE,"SEwAjyqW-bpiv-PUip-ikyk-NmgX0KRneyY1.bottom")])]})])],"derivedFrom":subQ7}),makeQuery(id+"Fx6GF23n7295V4c_1.boolean.opBoolean","SPLIT",EDGE,{"disambiguationData":[TD([makeQuery(id+"Fx6GF23n7295V4c_1.opExtrude","SWEPT_FACE",FACE,{"disambiguationData":[OSD([sQuery(id+"F88hl3kOj6oPiEs_1.wireOp",EDGE,"Me13D1SK-nVIm-EUZ4-u9ei-o20qw3bNrjn4.bottom")])]})])],"derivedFrom":subQ7}),makeQuery(id+"FdvM71XXdWx955j_1.opExtrude","SWEPT_EDGE",EDGE,{"disambiguationData":[OSD([sQuery(id+"FbjQCpLspRogReH_1.wireOp",EDGE,"f59d4a9d-c009-47c2-b376-d2920ef91a05.2"),sQuery(id+"FbjQCpLspRogReH_1.wireOp",EDGE,"yJWQzcis-0yOI-6z6T-26nz-SCj8SExaznUa")])]})]});}
            var Q6;
            {var subQ0=sQuery(id+"Fz5JRvEoveer3CH_1.wireOp",EDGE,"ed581da2-8291-48fe-b3ed-69cef9aa138a18.MirrorCS");var subQ1=sQuery(id+"Fz5JRvEoveer3CH_1.wireOp",EDGE,"ed581da2-8291-48fe-b3ed-69cef9aa138a14.MirrorCS");var subQ2=sQuery(id+"F0.wireOp",EDGE,"E0.left");var subQ4=sQuery(id+"Fz5JRvEoveer3CH_1.wireOp",EDGE,"ed581da2-8291-48fe-b3ed-69cef9aa138a29.MirrorCS");var subQ5=sQuery(id+"F0.wireOp",EDGE,"E3");var subQ7=makeQuery(id+"F6.opShell","OFFSET_EDGE",EDGE,{"disambiguationData":[OSD([subQ2,subQ5,subQ1,subQ0,subQ4])]});Q6=makeQuery(id+"FdvM71XXdWx955j_1.boolean.opBoolean","MERGE",EDGE,{"derivedFrom":[makeQuery(id+"Fx6GF23n7295V4c_1.boolean.opBoolean","SPLIT",EDGE,{"disambiguationData":[TD([makeQuery(id+"Fx6GF23n7295V4c_1.opExtrude","SWEPT_FACE",FACE,{"disambiguationData":[OSD([sQuery(id+"F88hl3kOj6oPiEs_1.wireOp",EDGE,"Me13D1SK-nVIm-EUZ4-u9ei-o20qw3bNrjn4.top")])]})])],"derivedFrom":subQ7}),makeQuery(id+"Fx6GF23n7295V4c_1.boolean.opBoolean","SPLIT",EDGE,{"disambiguationData":[TD([makeQuery(id+"Fx6GF23n7295V4c_1.opExtrude","SWEPT_FACE",FACE,{"disambiguationData":[OSD([sQuery(id+"F88hl3kOj6oPiEs_1.wireOp",EDGE,"SEwAjyqW-bpiv-PUip-ikyk-NmgX0KRneyY1.bottom")])]})])],"derivedFrom":subQ7}),makeQuery(id+"Fx6GF23n7295V4c_1.boolean.opBoolean","SPLIT",EDGE,{"disambiguationData":[TD([makeQuery(id+"Fx6GF23n7295V4c_1.opExtrude","SWEPT_FACE",FACE,{"disambiguationData":[OSD([sQuery(id+"F88hl3kOj6oPiEs_1.wireOp",EDGE,"Me13D1SK-nVIm-EUZ4-u9ei-o20qw3bNrjn4.bottom")])]})])],"derivedFrom":subQ7}),makeQuery(id+"FdvM71XXdWx955j_1.opExtrude","SWEPT_EDGE",EDGE,{"disambiguationData":[OSD([sQuery(id+"FbjQCpLspRogReH_1.wireOp",EDGE,"f59d4a9d-c009-47c2-b376-d2920ef91a05.2"),sQuery(id+"FbjQCpLspRogReH_1.wireOp",EDGE,"vCloutBl-IFQ8-1CZX-urJ5-Xu0XruTJAQ3o")])]})]});}
            var Q7;
            {var subQ0=sQuery(id+"Fz5JRvEoveer3CH_1.wireOp",EDGE,"ed581da2-8291-48fe-b3ed-69cef9aa138a21.MirrorCS");var subQ1=sQuery(id+"Fz5JRvEoveer3CH_1.wireOp",EDGE,"2a3d6910-861b-4cd5-9b03-4775f4baa4122.MirrorCS");var subQ2=sQuery(id+"F0.wireOp",EDGE,"E0.bottom");var subQ4=sQuery(id+"Fz5JRvEoveer3CH_1.wireOp",EDGE,"ed581da2-8291-48fe-b3ed-69cef9aa138a29.MirrorCS");var subQ5=sQuery(id+"F0.wireOp",EDGE,"E3");var subQ7=makeQuery(id+"F6.opShell","OFFSET_EDGE",EDGE,{"disambiguationData":[OSD([subQ2,subQ5,subQ1,subQ0,subQ4])]});Q7=makeQuery(id+"FdvM71XXdWx955j_1.boolean.opBoolean","MERGE",EDGE,{"derivedFrom":[makeQuery(id+"Fx6GF23n7295V4c_1.boolean.opBoolean","SPLIT",EDGE,{"disambiguationData":[TD([makeQuery(id+"Fx6GF23n7295V4c_1.opExtrude","SWEPT_FACE",FACE,{"disambiguationData":[OSD([sQuery(id+"F88hl3kOj6oPiEs_1.wireOp",EDGE,"Me13D1SK-nVIm-EUZ4-u9ei-o20qw3bNrjn4.top")])]})])],"derivedFrom":subQ7}),makeQuery(id+"Fx6GF23n7295V4c_1.boolean.opBoolean","SPLIT",EDGE,{"disambiguationData":[TD([makeQuery(id+"Fx6GF23n7295V4c_1.opExtrude","SWEPT_FACE",FACE,{"disambiguationData":[OSD([sQuery(id+"F88hl3kOj6oPiEs_1.wireOp",EDGE,"SEwAjyqW-bpiv-PUip-ikyk-NmgX0KRneyY1.bottom")])]})])],"derivedFrom":subQ7}),makeQuery(id+"Fx6GF23n7295V4c_1.boolean.opBoolean","SPLIT",EDGE,{"disambiguationData":[TD([makeQuery(id+"Fx6GF23n7295V4c_1.opExtrude","SWEPT_FACE",FACE,{"disambiguationData":[OSD([sQuery(id+"F88hl3kOj6oPiEs_1.wireOp",EDGE,"Me13D1SK-nVIm-EUZ4-u9ei-o20qw3bNrjn4.bottom")])]})])],"derivedFrom":subQ7}),makeQuery(id+"FdvM71XXdWx955j_1.opExtrude","SWEPT_EDGE",EDGE,{"disambiguationData":[OSD([sQuery(id+"FbjQCpLspRogReH_1.wireOp",EDGE,"f59d4a9d-c009-47c2-b376-d2920ef91a05.4"),sQuery(id+"FbjQCpLspRogReH_1.wireOp",EDGE,"vCloutBl-IFQ8-1CZX-urJ5-Xu0XruTJAQ3o")])]})]});}
            fillet(context, id + "F10", {"entities" : qUnion([Q0, Q1, Q2, Q3, Q4, Q5, Q6, Q7]), "radius" : 1 * mm, "tangentPropagation" : true, "allowEdgeOverflow" : false});
        }
    });
